# Revit family: LAMP_FIL 70 PRISMATIC SUSPENDED
name_source: partatom
category: Luminarias
revit_build: Autodesk Revit 2015 (Build: 20140606_1530(x64)
units: mm (PartAtom-declared; Revit-internal decimal feet)

## types (16) — shared parameters
CRI = 80
Cambio de temperatura de color de luz atenuada = <Ninguno>
Comentarios de tipo = Availability of switching between accessories through visibility parameters when placed in a project.
Fabricante = LAMP
Filtro de color = 16777215
Gear = Electronic
IEE = A+
IFC Clasificación = Light Fixture
Installation instructions = https://www.lamp.es
Insulation class = I
LED Lifetime = 50000 L80 B10
Last update = 14/08/2020
Luminaire type = Indoor - Modular System
Lámpara = LED MID-POWER
MacAdam = 3
Manufacturer URL = http://www.lamp.es
Manufacturer country = Spain
Manufacturer name = LAMP
Material Difusor = LAMP_PC Difusor Prismático Fil
Model explanation = Availability of switching between accessories through visibility parameters when placed in a project.
Power Supply = 220-240V 50-60Hz
Product URL = https://www.lamp.es
Product datasheet = https://www.lamp.es
Protection rating = IP42, IK06
Type = MID POWER PHILIPS
Ángulo de inclinación = 90,00°

## per-type parameters (varying)
| type | Archivo de red fotométrica | Descripción | Dimensiones | Efficacy | Finish | Largo | Longitud de línea de emisión | Material Perfil | Material codo | Modelo | Plum | Power | Product code | UniClass 1.4 Code | UniClass 2.0 Code | Weight |
| 1162MM 2600LM 3000K GREY | 14741603.IES | FIL 70 PRISM SUS 2600 WW GR. | 1.162x70x70mm | 114 lm/W | Gloss Grey | 1162 mm  [stored 3.81234 ft] | 1162 mm  [stored 3.81234 ft] | LAMP_Aluminio Perfil Fil GR | LAMP_Aluminio Perfil Fil GR | F71SF120LOPR830NG
F71SF120LOPR830NG | 19 W | 17 W | F71SF120LOPR830NG
F71SF120LOPR830NG | F71SF120LOPR830NG
F71SF120LOPR830NG | F71SF120LOPR830NG
F71SF120LOPR830NG | 2,63 kg |
| 1162MM 2600LM 3000K WHITE | 14741600.IES | FIL 70 PRISM SUS 2600 WW WH. | 1.162x70x70mm | 114 lm/W | Matt White | 1162 mm  [stored 3.81234 ft] | 1162 mm  [stored 3.81234 ft] | LAMP_Aluminio Perfil Fil BL | LAMP_Aluminio Perfil Fil BL | F71SF120LOPR830NW | 19 W | 17 W | F71SF120LOPR830NW | F71SF120LOPR830NW | F71SF120LOPR830NW | 2,63 kg |
| 1162MM 2600LM 4000K GREY | 14740603.IES | FIL 70 PRISM SUS 2600 NW GR. | 1.162x70x70mm | 119 lm/W | Gloss Grey | 1162 mm  [stored 3.81234 ft] | 1162 mm  [stored 3.81234 ft] | LAMP_Aluminio Perfil Fil GR | LAMP_Aluminio Perfil Fil GR | F71SF120LOPR840NG | 19 W | 17 W | F71SF120LOPR840NG | F71SF120LOPR840NG | F71SF120LOPR840NG | 2,63 kg |
| 1162MM 2600LM 4000K WHITE | 14740600.IES | FIL 70 PRISM SUS 2600 NW WH. | 1.162x70x70mm | 119 lm/W | Matt White | 1162 mm  [stored 3.81234 ft] | 1162 mm  [stored 3.81234 ft] | LAMP_Aluminio Perfil Fil BL | LAMP_Aluminio Perfil Fil BL | F71SF120LOPR840NW | 19 W | 17 W | F71SF120LOPR840NW | F71SF120LOPR840NW | F71SF120LOPR840NW | 2,63 kg |
| 1162MM 4400LM 3000K GREY | 14741613.IES | FIL 70 PRISM SUS 4400 WW GR. | 1.162x70x70mm | 117 lm/W | Gloss Grey | 1162 mm  [stored 3.81234 ft] | 1162 mm  [stored 3.81234 ft] | LAMP_Aluminio Perfil Fil GR | LAMP_Aluminio Perfil Fil GR | F71SF120HOPR830NG | 31 W | 28 W | F71SF120HOPR830NG | F71SF120HOPR830NG | F71SF120HOPR830NG | 2,63 kg |
| 1162MM 4400LM 3000K WHITE | 14741610.IES | FIL 70 PRISM SUS 4400 WW WH. | 1.162x70x70mm | 117 lm/W | Matt White | 1162 mm  [stored 3.81234 ft] | 1162 mm  [stored 3.81234 ft] | LAMP_Aluminio Perfil Fil BL | LAMP_Aluminio Perfil Fil BL | F71SF120HOPR830NW | 31 W | 28 W | F71SF120HOPR830NW | F71SF120HOPR830NW | F71SF120HOPR830NW | 2,63 kg |
| 1162MM 4400LM 4000K GREY | 14740613.IES | FIL 70 PRISM SUS 4400 NW GR | 1.162x70x70mm | 122 lm/W | Gloss Grey | 1162 mm  [stored 3.81234 ft] | 1162 mm  [stored 3.81234 ft] | LAMP_Aluminio Perfil Fil GR | LAMP_Aluminio Perfil Fil GR | F71SF120HOPR840NG | 31 W | 28 W | F71SF120HOPR840NG | F71SF120HOPR840NG | F71SF120HOPR840NG | 2,63 kg |
| 1162MM 4400LM 4000K WHITE | 14740610.IES | FIL 70 PRISM SUS 4400 NW WH. | 1.162x70x70mm | 122 lm/W | Gloss Grey | 1162 mm  [stored 3.81234 ft] | 1162 mm  [stored 3.81234 ft] | LAMP_Aluminio Perfil Fil BL | LAMP_Aluminio Perfil Fil BL | F71SF120HOPR840NW | 31 W | 28 W | F71SF120HOPR840NW | F71SF120HOPR840NW | F71SF120HOPR840NW | 2,63 kg |
| 1743MM 3900LM 3000K GREY | 14741623.IES | FIL 70 PRISM SUS 3900 WW GR. | 1.743x70x70mm | 124 lm/W | Gloss Grey | 1743 mm  [stored 5.7185 ft] | 1743 mm  [stored 5.7185 ft] | LAMP_Aluminio Perfil Fil GR | LAMP_Aluminio Perfil Fil GR | F71SF170LOPR830NG | 30 W | 25 W | F71SF170LOPR830NG | F71SF170LOPR830NG | F71SF170LOPR830NG | 4,15 kg |
| 1743MM 3900LM 3000K WHITE | 14741620.IES | FIL 70 PRISM SUS 3900 WW WH. | 1.743x70x70mm | 117 lm/W | Matt White | 1743 mm  [stored 5.7185 ft] | 1743 mm  [stored 5.7185 ft] | LAMP_Aluminio Perfil Fil BL | LAMP_Aluminio Perfil Fil BL | F71SF170LOPR830NW | 30 W | 25 W | F71SF170LOPR830NW | F71SF170LOPR830NW | F71SF170LOPR830NW | 4,15 kg |
| 1743MM 3900LM 4000K GREY | 14740623.IES | FIL 70 PRISM SUS 3900 NW GR. | 1.743x70x70mm | 129 lm/W | Gloss Grey | 1743 mm  [stored 5.7185 ft] | 1743 mm  [stored 5.7185 ft] | LAMP_Aluminio Perfil Fil GR | LAMP_Aluminio Perfil Fil GR | F71SF170LOPR840NG | 30 W | 25 W | F71SF170LOPR840NG | F71SF170LOPR840NG | F71SF170LOPR840NG | 4,15 kg |
| 1743MM 3900LM 4000K WHITE | 14740620.IES | FIL 70 PRISM SUS 3900 NW WH. | 1.743x70x70mm | 129 lm/W | Matt White | 1743 mm  [stored 5.7185 ft] | 1743 mm  [stored 5.7185 ft] | LAMP_Aluminio Perfil Fil BL | LAMP_Aluminio Perfil Fil BL | F71SF170LOPR840NW | 30 W | 25 W | F71SF170LOPR840NW | F71SF170LOPR840NW | F71SF170LOPR840NW | 4,15 kg |
| 1743MM 6600LM 3000K GREY | 14741633.IES | FIL 70 PRISM SUS 6600 WW GR. | 1.743x70x70mm | 123 lm/W | Gloss Grey | 1743 mm  [stored 5.7185 ft] | 1743 mm  [stored 5.7185 ft] | LAMP_Aluminio Perfil Fil GR | LAMP_Aluminio Perfil Fil GR | F71SF170HOPR830NG | 46 W | 41 W | F71SF170HOPR830NG | F71SF170HOPR830NG | F71SF170HOPR830NG | 4,15 kg |
| 1743MM 6600LM 3000K WHITE | 14741630.IES | FIL 70 PRISM SUS 6600 WW WH. | 1.743x70x70mm | 123 lm/W | Matt White | 1743 mm  [stored 5.7185 ft] | 1743 mm  [stored 5.7185 ft] | LAMP_Aluminio Perfil Fil BL | LAMP_Aluminio Perfil Fil BL | F71SF170HOPR830NW | 46 W | 41 W | F71SF170HOPR830NW | F71SF170HOPR830NW | F71SF170HOPR830NW | 4,15 kg |
| 1743MM 6600LM 4000K GREY | 14740633.IES | FIL 70 PRISM SUS 6600 NW GR. | 1.743x70x70mm | 127 lm/W | Gloss Grey | 1743 mm  [stored 5.7185 ft] | 1743 mm  [stored 5.7185 ft] | LAMP_Aluminio Perfil Fil GR | LAMP_Aluminio Perfil Fil GR | F71SF170HOPR840NG | 46 W | 41 W | F71SF170HOPR840NG | F71SF170HOPR840NG | F71SF170HOPR840NG | 4,15 kg |
| 1743MM 6600LM 4000K WHITE | 14740630.IES | FIL 70 PRISM SUS 6600 NW WH. | 1.743x70x70mm | 127 lm/W | Matt White | 1743 mm  [stored 5.7185 ft] | 1743 mm  [stored 5.7185 ft] | LAMP_Aluminio Perfil Fil BL | LAMP_Aluminio Perfil Fil BL | F71SF170HOPR840NW | 46 W | 41 W | F71SF170HOPR840NW | F71SF170HOPR840NW | F71SF170HOPR840NW | 4,15 kg |

note: [stored X ft] marks values corroborated as IEEE doubles in the binary element streams (Revit-internal decimal feet)

## geometry (parser evidence)
native form markers: Blend x5
no freeform markers — native parametric forms only
